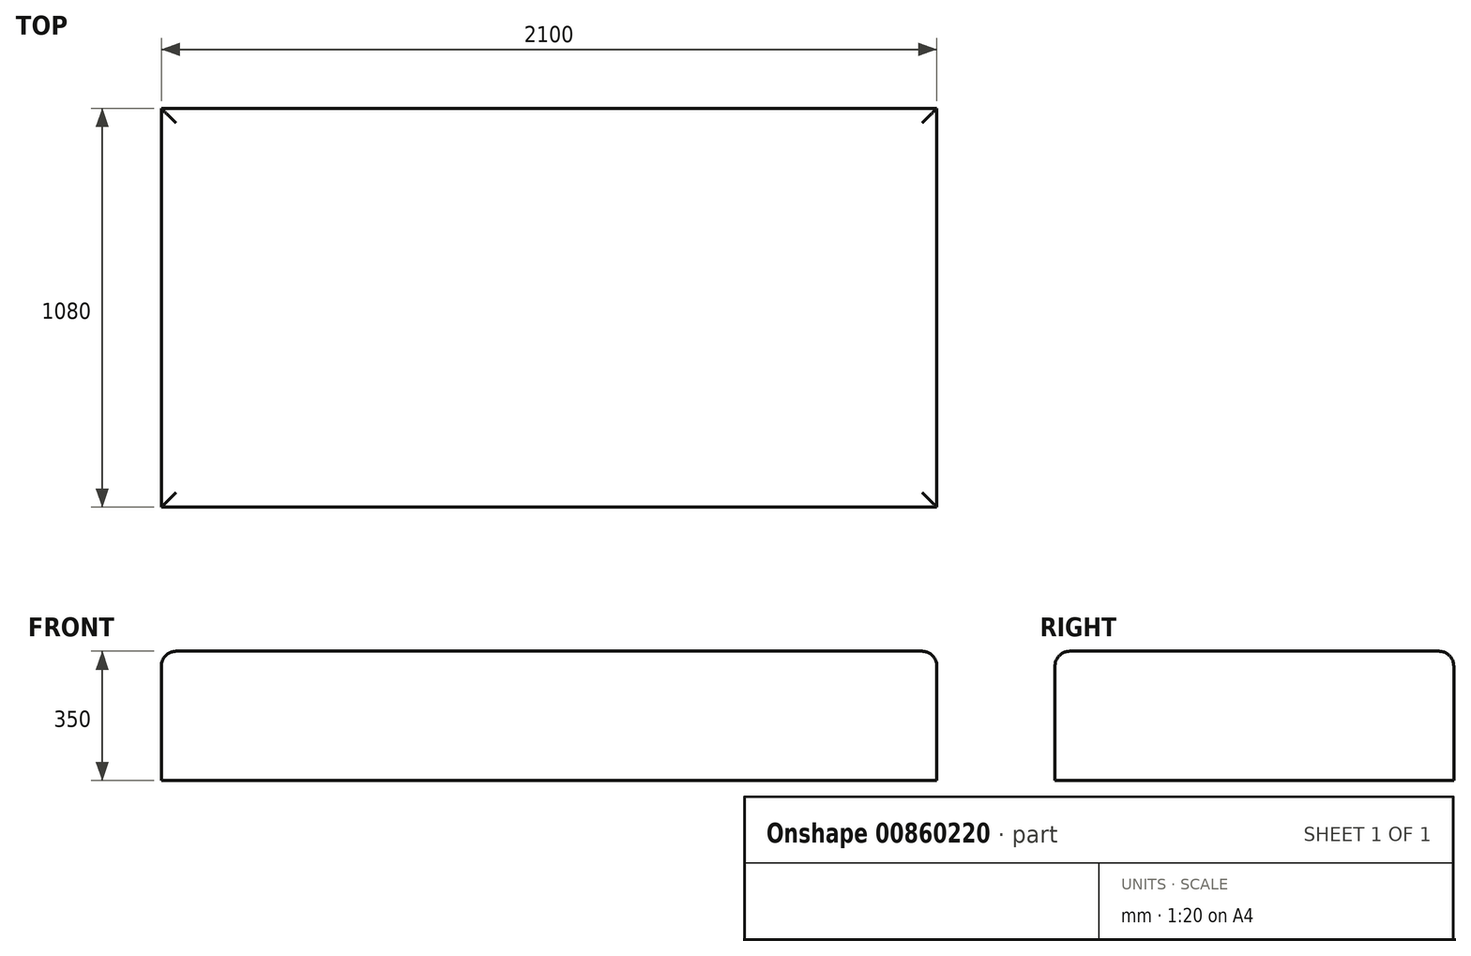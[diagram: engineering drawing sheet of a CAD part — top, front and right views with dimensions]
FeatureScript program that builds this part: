
annotation { "Feature Type Name" : "Feature", "Feature Type Description" : "" }
export const myFeature = defineFeature(function(context is Context, id is Id, definition is map)
    precondition{}
    {
        {
            var Q0;
            Q0=qCreatedBy(makeId("Top.planeOp"),FACE);
            var sketch = newSketch(context, id + "F0", { "sketchPlane" : qUnion([Q0])});
            skLineSegment(sketch, "E0.bottom", {"start": v(0, 0) * mm, "end": v(2100, 0) * mm});
            skLineSegment(sketch, "E0.top", {"start": v(0, 1080) * mm, "end": v(2100, 1080) * mm});
            skLineSegment(sketch, "E0.left", {"start": v(0, 0) * mm, "end": v(0, 1080) * mm});
            skLineSegment(sketch, "E0.right", {"start": v(2100, 0) * mm, "end": v(2100, 1080) * mm});
            skSolve(sketch);
        }
        {
            var Q0;
            Q0=makeQuery(id+"F0.imprint","IMPRINT",FACE,{"disambiguationData":[TD([[makeQuery(id+"F0.imprint","IMPRINT",EDGE,{"derivedFrom":sQuery(id+"F0.wireOp",EDGE,"E0.bottom")}),1.0]])]});
            var Q1;
            Q1 = qSketchRegion(id + "F0", true);
            extrude(context, id + "F1", {"entities" : qUnion([Q0, Q1]), "depth" : 350 * mm, "offsetDistance" : 25 * mm});
        }
        {
            var Q0;
            Q0=makeQuery(id+"F1.opExtrude","CAP_FACE",FACE,{"disambiguationData":[OSD([sQuery(id+"F0.wireOp",EDGE,"E0.bottom"),sQuery(id+"F0.wireOp",EDGE,"E0.top"),sQuery(id+"F0.wireOp",EDGE,"E0.left"),sQuery(id+"F0.wireOp",EDGE,"E0.right")])],"isStart":false});
            fillet(context, id + "F2", {"entities" : qUnion([Q0]), "radius" : 40 * mm, "tangentPropagation" : true, "allowEdgeOverflow" : false});
        }
    });
